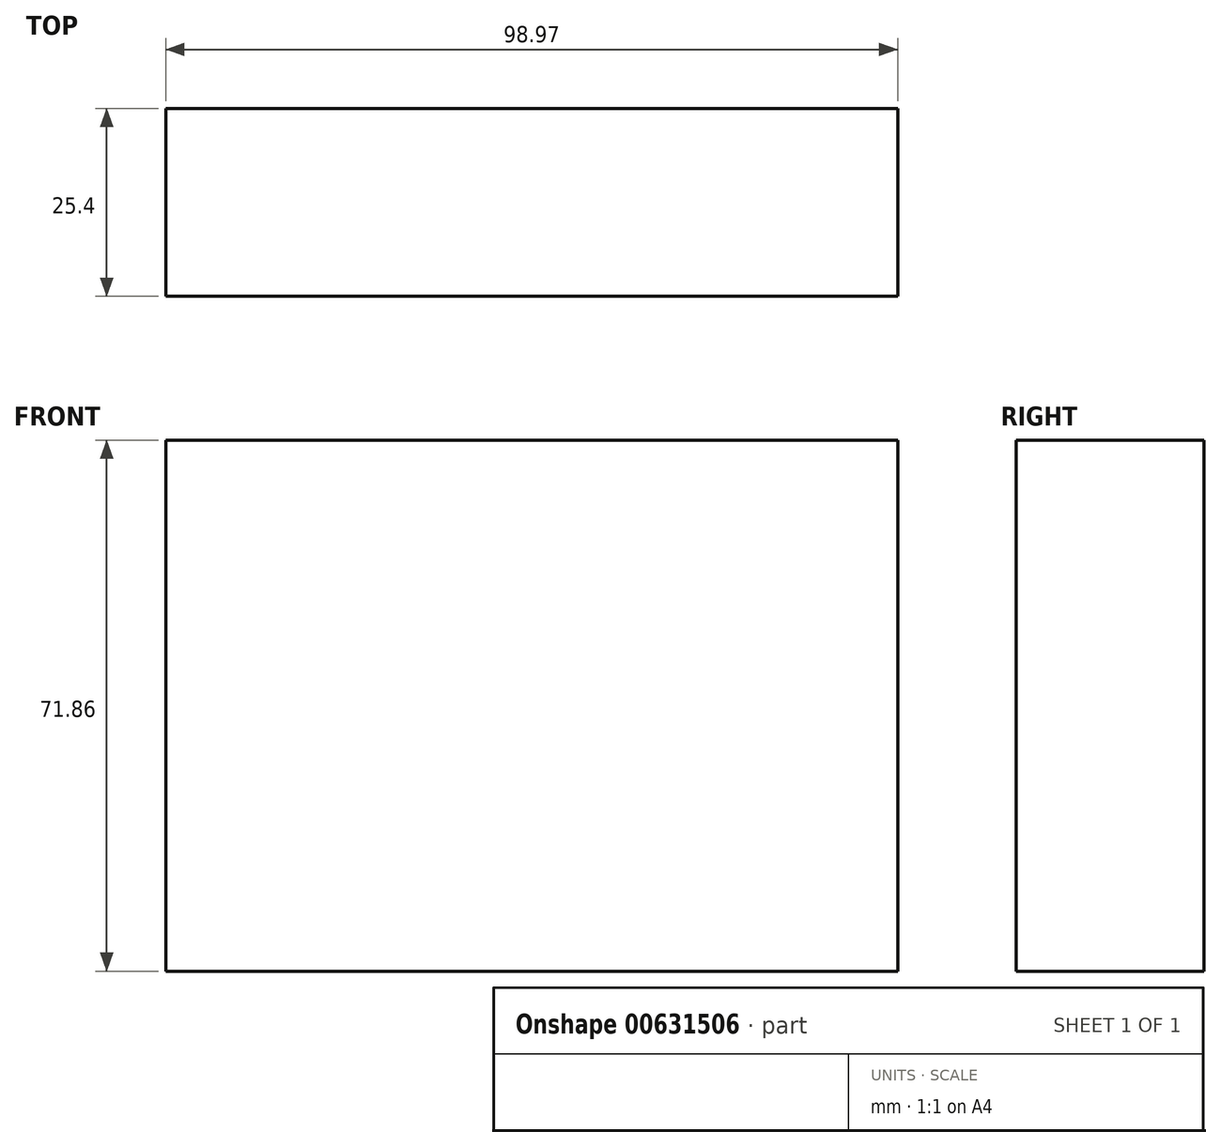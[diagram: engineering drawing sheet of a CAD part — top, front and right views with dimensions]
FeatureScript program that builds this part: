
annotation { "Feature Type Name" : "Feature", "Feature Type Description" : "" }
export const myFeature = defineFeature(function(context is Context, id is Id, definition is map)
    precondition{}
    {
        {
            var Q0;
            Q0=qCreatedBy(makeId("Front.planeOp"),FACE);
            var sketch = newSketch(context, id + "F0", { "sketchPlane" : qUnion([Q0])});
            skSolve(sketch);
        }
        {
            var Q0;
            Q0=qCreatedBy(makeId("Front.planeOp"),FACE);
            var sketch = newSketch(context, id + "F1", { "sketchPlane" : qUnion([Q0])});
            skLineSegment(sketch, "E0.bottom", {"start": v(-49.2, 35.74) * mm, "end": v(49.77, 35.74) * mm});
            skLineSegment(sketch, "E0.top", {"start": v(-49.2, -36.12) * mm, "end": v(49.77, -36.12) * mm});
            skLineSegment(sketch, "E0.left", {"start": v(-49.2, 35.74) * mm, "end": v(-49.2, -36.12) * mm});
            skLineSegment(sketch, "E0.right", {"start": v(49.77, 35.74) * mm, "end": v(49.77, -36.12) * mm});
            skSolve(sketch);
        }
        {
            var Q0;
            Q0 = qSketchRegion(id + "F0", true);
            var Q1;
            Q1 = qSketchRegion(id + "F1", true);
            extrude(context, id + "F2", {"entities" : qUnion([Q0, Q1]), "depth" : 25.4 * mm, "offsetDistance" : 25.4 * mm});
        }
    });
